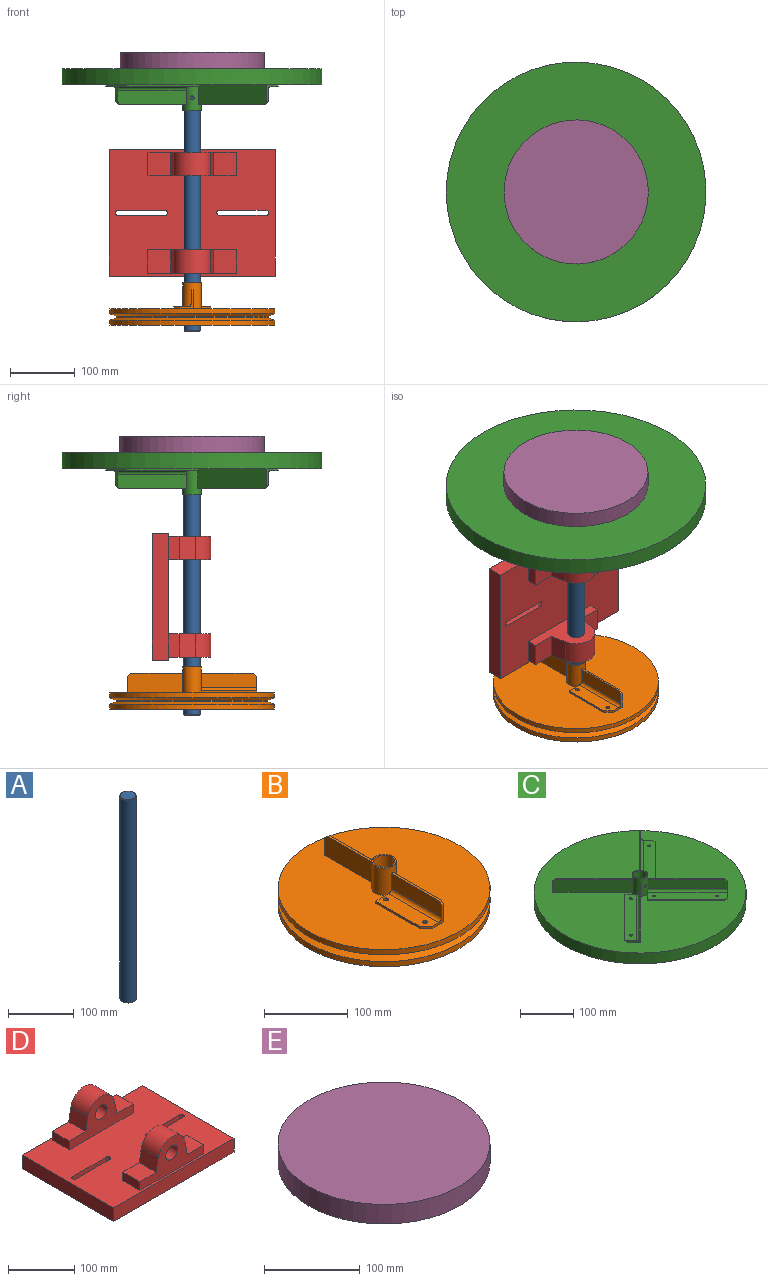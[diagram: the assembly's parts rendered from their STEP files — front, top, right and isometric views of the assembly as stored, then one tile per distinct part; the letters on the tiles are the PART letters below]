
ASSEMBLY  parts=5 mates=4
PART A: 5 faces, bbox 25x25x380 mm
  f0: cylinder r=12.5mm len=378mm, axis (0,0,-1), area 29688.1mm2, adj f3,f4
  f1: plane 23x23mm, normal (0,0,1), area 415.5mm2, adj f3
  f2: plane 23x23mm, normal (0,0,-1), area 415.5mm2, adj f4
  f3: cone r=11.5mm half-angle=45deg, axis (0,0,-1), area 106.6mm2, adj f0,f1
  f4: cone r=12.5mm half-angle=45deg, axis (0,0,1), area 106.6mm2, adj f0,f2
PART B: 41 faces, bbox 254x254x65 mm
  f0: plane 254x254mm, normal (0,0,1), area 45010.4mm2, adj f1,f8,f9,f10,f14,f15,f19,f21
  f1: cylinder r=127mm len=254mm, axis (0,0,1), area 5984.7mm2, adj f0,f2
  f2: cone r=127mm half-angle=70deg, axis (0,0,1), area 8157.4mm2, adj f1,f3
  f3: cylinder r=117mm len=234mm, axis (0,0,1), area 2000mm2, adj f2,f4
  f4: cone r=127mm half-angle=70deg, axis (0,0,-1), area 8157.4mm2, adj f3,f5
  f5: cylinder r=127mm len=254mm, axis (0,0,1), area 5984.7mm2, adj f4,f6
  f6: plane 254x254mm, normal (0,0,-1), area 50179.9mm2, adj f5,f7
  f7: cylinder r=12.5mm len=65mm, axis (0,0,1), area 5076.6mm2, adj f6,f35,f36
  f8: plane 30x27.3mm, normal (0,-1,0), area 95.3mm2, adj f0,f11,f12,f13,f14,f16,f21
  f9: plane 30x0.3mm, normal (0,-1,0), area 8.9mm2, adj f0,f10,f11,f21
  f10: plane 85x30mm, normal (-1,0,0), area 2537.5mm2, adj f0,f9,f11,f15,f20
  f11: plane 80x3mm, normal (0,0,1), area 239.9mm2, adj f8,f9,f10,f12,f20,f21
  f12: plane 85x22mm, normal (1,0,0), area 1857.5mm2, adj f8,f11,f15,f16,f20
  f13: plane 85x22mm, normal (0,0,1), area 1763.5mm2, adj f8,f14,f15,f16,f17,f18,f19
  f14: plane 75x3mm, normal (1,0,0), area 225mm2, adj f0,f8,f13,f19
  f15: plane 25x20mm, normal (0,1,0), area 131.4mm2, adj f0,f10,f12,f13,f16,f19,f20
  f16: cylinder r=5mm len=85mm, axis (0,1,0), area 667.6mm2, adj f8,f12,f13,f15
  f17: cylinder r=3mm len=6mm, axis (0,0,1), area 56.5mm2, adj f13,f38
  f18: cylinder r=3mm len=6mm, axis (0,0,1), area 56.5mm2, adj f13,f39
  f19: plane 10x10mm, normal (0.71,0.71,0), area 42.4mm2, adj f0,f13,f14,f15
  f20: plane 5x5mm, normal (0,0.71,0.71), area 21.2mm2, adj f10,f11,f12,f15
  f21: cylinder r=14.5mm len=40mm, axis (0,0,-1), area 3471.2mm2, adj f0,f8,f9,f11,f22,f23,f25,f35
  f22: plane 30x27.3mm, normal (0,1,0), area 95.3mm2, adj f0,f21,f25,f26,f27,f28,f30
  f23: plane 30x0.3mm, normal (0,1,0), area 8.9mm2, adj f0,f21,f24,f25
  f24: plane 85x30mm, normal (1,0,0), area 2537.5mm2, adj f0,f23,f25,f29,f34
  f25: plane 80x3mm, normal (0,0,1), area 239.9mm2, adj f21,f22,f23,f24,f26,f34
  f26: plane 85x22mm, normal (-1,0,0), area 1857.5mm2, adj f22,f25,f29,f30,f34
  f27: plane 85x22mm, normal (0,0,1), area 1763.5mm2, adj f22,f28,f29,f30,f31,f32,f33
  f28: plane 75x3mm, normal (-1,0,0), area 225mm2, adj f0,f22,f27,f33
  f29: plane 25x20mm, normal (0,-1,0), area 131.4mm2, adj f0,f24,f26,f27,f30,f33,f34
  f30: cylinder r=5mm len=85mm, axis (0,-1,0), area 667.6mm2, adj f22,f26,f27,f29
  f31: cylinder r=3mm len=6mm, axis (0,0,1), area 56.5mm2, adj f27,f40
  f32: cylinder r=3mm len=6mm, axis (0,0,1), area 56.5mm2, adj f27,f37
  f33: plane 10x10mm, normal (-0.71,-0.71,0), area 42.4mm2, adj f0,f27,f28,f29
  f34: plane 5x5mm, normal (0,-0.71,0.71), area 21.2mm2, adj f24,f25,f26,f29
  f35: plane 29x29mm, normal (0,0,1), area 169.6mm2, adj f7,f21
  f36: cylinder r=3mm len=6mm, axis (-1,0,0), area 38.2mm2, adj f7,f21
  f37: plane 6x6mm, normal (0,0,1), area 28.3mm2, adj f32
  f38: plane 6x6mm, normal (0,0,1), area 28.3mm2, adj f17
  f39: plane 6x6mm, normal (0,0,1), area 28.3mm2, adj f18
  f40: plane 6x6mm, normal (0,0,1), area 28.3mm2, adj f31
PART C: 64 faces, bbox 400x400x65 mm
  f0: plane 106.05x106.05mm, normal (-0.71,-0.71,0), area 3287mm2, adj f1,f16,f19,f23,f59
  f1: cylinder r=5mm len=109.6mm, axis (0.71,-0.71,0), area 1178.1mm2, adj f0,f9,f17,f19,f59
  f2: plane 106.05x106.05mm, normal (0.71,0.71,0), area 3287mm2, adj f3,f26,f29,f33,f59
  f3: cylinder r=5mm len=109.6mm, axis (-0.71,0.71,0), area 1178.1mm2, adj f2,f11,f27,f29,f59
  f4: cylinder r=5mm len=109.6mm, axis (-0.71,-0.71,0), area 1178.1mm2, adj f5,f12,f42,f44,f59
  f5: plane 106.05x106.05mm, normal (-0.71,0.71,0), area 3287mm2, adj f4,f38,f42,f45,f59
  f6: cylinder r=5mm len=109.6mm, axis (0.71,0.71,0), area 1178.1mm2, adj f7,f14,f52,f54,f59
  f7: plane 106.05x106.05mm, normal (0.71,-0.71,0), area 3287mm2, adj f6,f48,f52,f55,f59
  f8: plane 106.05x106.05mm, normal (0.71,0.71,0), area 4486.8mm2, adj f16,f19,f23,f56,f59
  f9: plane 18.95x18.95mm, normal (-0.71,0.71,0), area 85mm2, adj f1,f17,f18,f56,f59
  f10: plane 106.05x106.05mm, normal (-0.71,-0.71,0), area 4486.8mm2, adj f26,f29,f33,f56,f59
  f11: plane 18.95x18.95mm, normal (0.71,-0.71,0), area 85mm2, adj f3,f27,f28,f56,f59
  f12: plane 18.95x18.95mm, normal (0.71,0.71,0), area 85mm2, adj f4,f43,f44,f56,f59
  f13: plane 106.05x106.05mm, normal (0.71,-0.71,0), area 4486.8mm2, adj f38,f42,f45,f56,f59
  f14: plane 18.95x18.95mm, normal (-0.71,-0.71,0), area 85mm2, adj f6,f53,f54,f56,f59
  f15: plane 106.05x106.05mm, normal (-0.71,0.71,0), area 4486.8mm2, adj f48,f52,f55,f56,f59
  f16: plane 104.64x104.64mm, normal (0,0,1), area 434.8mm2, adj f0,f8,f23,f59
  f17: plane 121.62x118.09mm, normal (0,0,1), area 3231mm2, adj f1,f9,f18,f19,f20,f21,f22
  f18: plane 102.53x102.53mm, normal (-0.71,-0.71,0), area 435mm2, adj f9,f17,f22,f56
  f19: plane 25x17.68mm, normal (0.71,-0.71,0), area 146.4mm2, adj f0,f1,f8,f17,f22,f23,f56
  f20: cylinder r=3mm len=6mm, axis (0,0,1), area 56.5mm2, adj f17,f58
  f21: cylinder r=3mm len=6mm, axis (0,0,1), area 56.5mm2, adj f17,f57
  f22: plane 7.07x3mm, normal (0,-1,0), area 21.2mm2, adj f17,f18,f19,f56
  f23: plane 5.66x5.66mm, normal (0.5,-0.5,0.71), area 21.2mm2, adj f0,f8,f16,f19
  f24: plane 6x6mm, normal (0,0,1), area 28.3mm2, adj f51
  f25: plane 6x6mm, normal (0,0,1), area 28.3mm2, adj f50
  f26: plane 104.64x104.64mm, normal (0,0,1), area 434.8mm2, adj f2,f10,f33,f59
  f27: plane 121.62x118.09mm, normal (0,0,1), area 3231mm2, adj f3,f11,f28,f29,f30,f31,f32
  f28: plane 102.53x102.53mm, normal (0.71,0.71,0), area 435mm2, adj f11,f27,f32,f56
  f29: plane 25x17.68mm, normal (-0.71,0.71,0), area 146.4mm2, adj f2,f3,f10,f27,f32,f33,f56
  f30: cylinder r=3mm len=6mm, axis (0,0,1), area 56.5mm2, adj f27,f47
  f31: cylinder r=3mm len=6mm, axis (0,0,1), area 56.5mm2, adj f27,f46
  f32: plane 7.07x3mm, normal (0,1,0), area 21.2mm2, adj f27,f28,f29,f56
  f33: plane 5.66x5.66mm, normal (-0.5,0.5,0.71), area 21.2mm2, adj f2,f10,f26,f29
  f34: plane 6x6mm, normal (0,0,1), area 28.3mm2, adj f40
  f35: plane 6x6mm, normal (0,0,1), area 28.3mm2, adj f41
  f36: cylinder r=200mm len=400mm, axis (0,0,1), area 31415.9mm2, adj f37,f56
  f37: plane 400x400mm, normal (0,0,-1), area 125663.7mm2, adj f36
  f38: plane 5.66x5.66mm, normal (-0.5,-0.5,0.71), area 21.2mm2, adj f5,f13,f42,f45
  f39: plane 7.07x3mm, normal (-1,0,0), area 21.2mm2, adj f42,f43,f44,f56
  f40: cylinder r=3mm len=6mm, axis (0,0,1), area 56.5mm2, adj f34,f44
  f41: cylinder r=3mm len=6mm, axis (0,0,1), area 56.5mm2, adj f35,f44
  f42: plane 25x17.68mm, normal (-0.71,-0.71,0), area 146.4mm2, adj f4,f5,f13,f38,f39,f44,f56
  f43: plane 102.53x102.53mm, normal (-0.71,0.71,0), area 435mm2, adj f12,f39,f44,f56
  f44: plane 121.62x118.09mm, normal (0,0,1), area 3231mm2, adj f4,f12,f39,f40,f41,f42,f43
  f45: plane 104.64x104.64mm, normal (0,0,1), area 434.8mm2, adj f5,f13,f38,f59
  f46: plane 6x6mm, normal (0,0,1), area 28.3mm2, adj f31
  f47: plane 6x6mm, normal (0,0,1), area 28.3mm2, adj f30
  f48: plane 5.66x5.66mm, normal (0.5,0.5,0.71), area 21.2mm2, adj f7,f15,f52,f55
  f49: plane 7.07x3mm, normal (1,0,0), area 21.2mm2, adj f52,f53,f54,f56
  f50: cylinder r=3mm len=6mm, axis (0,0,1), area 56.5mm2, adj f25,f54
  f51: cylinder r=3mm len=6mm, axis (0,0,1), area 56.5mm2, adj f24,f54
  f52: plane 25x17.68mm, normal (0.71,0.71,0), area 146.4mm2, adj f6,f7,f15,f48,f49,f54,f56
  f53: plane 102.53x102.53mm, normal (0.71,-0.71,0), area 435mm2, adj f14,f49,f54,f56
  f54: plane 121.62x118.09mm, normal (0,0,1), area 3231mm2, adj f6,f14,f49,f50,f51,f52,f53
  f55: plane 104.64x104.64mm, normal (0,0,1), area 434.8mm2, adj f7,f15,f48,f59
  f56: plane 400x400mm, normal (0,0,1), area 107058.6mm2, adj f8,f9,f10,f11,f12,f13,f14,f15
  f57: plane 6x6mm, normal (0,0,1), area 28.3mm2, adj f21
  f58: plane 6x6mm, normal (0,0,1), area 28.3mm2, adj f20
  f59: cylinder r=14.45mm len=40mm, axis (0,0,-1), area 3236.8mm2, adj f0,f1,f2,f3,f4,f5,f6,f7
  f60: cylinder r=12.5mm len=40mm, axis (0,0,-1), area 3113.1mm2, adj f61,f62,f63
  f61: plane 28.9x28.9mm, normal (0,0,1), area 165.1mm2, adj f59,f60
  f62: cylinder r=3mm len=6mm, axis (0,-1,0), area 37.2mm2, adj f59,f60
  f63: plane 25x25mm, normal (0,0,1), area 490.9mm2, adj f60
PART D: 34 faces, bbox 256x195x90 mm
  f0: plane 36x35.03mm, normal (0,0,1), area 1260.9mm2, adj f1,f6,f8,f9
  f1: plane 36x16mm, normal (-1,0,0), area 576mm2, adj f0,f8,f9,f10
  f2: plane 36x16mm, normal (1,0,0), area 576mm2, adj f3,f8,f9,f10
  f3: plane 36x35.03mm, normal (0,0,1), area 1260.9mm2, adj f2,f4,f8,f9
  f4: plane 36x25.04mm, normal (0.98,0,0.17), area 915.2mm2, adj f3,f5,f8,f9
  f5: cylinder r=29mm len=57.12mm, axis (0,-1,0), area 2915.4mm2, adj f4,f6,f8,f9
  f6: plane 36x25.04mm, normal (-0.98,0,0.17), area 915.2mm2, adj f0,f5,f8,f9
  f7: cylinder r=12.5mm len=36mm, axis (0,-1,0), area 2827.4mm2, adj f8,f9
  f8: plane 136x65mm, normal (0,1,0), area 4256.1mm2, adj f0,f1,f2,f3,f4,f5,f6,f7
  f9: plane 136x65mm, normal (0,-1,0), area 4256.1mm2, adj f0,f1,f2,f3,f4,f5,f6,f7
  f10: plane 256x195mm, normal (0,0,1), area 38875.5mm2, adj f1,f2,f8,f9,f12,f13,f19,f20
  f11: plane 36x35.03mm, normal (0,0,1), area 1260.9mm2, adj f12,f17,f19,f20
  f12: plane 36x16mm, normal (-1,0,0), area 576mm2, adj f10,f11,f19,f20
  f13: plane 36x16mm, normal (1,0,0), area 576mm2, adj f10,f14,f19,f20
  f14: plane 36x35.03mm, normal (0,0,1), area 1260.9mm2, adj f13,f15,f19,f20
  f15: plane 36x25.04mm, normal (0.98,0,0.17), area 915.2mm2, adj f14,f16,f19,f20
  f16: cylinder r=29mm len=57.12mm, axis (0,-1,0), area 2915.4mm2, adj f15,f17,f19,f20
  f17: plane 36x25.04mm, normal (-0.98,0,0.17), area 915.2mm2, adj f11,f16,f19,f20
  f18: cylinder r=12.5mm len=36mm, axis (0,-1,0), area 2827.4mm2, adj f19,f20
  f19: plane 136x65mm, normal (0,1,0), area 4256.1mm2, adj f10,f11,f12,f13,f14,f15,f16,f17
  f20: plane 136x65mm, normal (0,-1,0), area 4256.1mm2, adj f10,f11,f12,f13,f14,f15,f16,f17
  f21: cylinder r=4mm len=25mm, axis (0,0,1), area 314.2mm2, adj f10,f22,f32,f33
  f22: plane 72x25mm, normal (0,-1,0), area 1800mm2, adj f10,f21,f23,f33
  f23: cylinder r=4mm len=25mm, axis (0,0,1), area 314.2mm2, adj f10,f22,f32,f33
  f24: plane 72x25mm, normal (0,-1,0), area 1800mm2, adj f10,f25,f30,f33
  f25: cylinder r=4mm len=25mm, axis (0,0,1), area 314.2mm2, adj f10,f24,f26,f33
  f26: plane 72x25mm, normal (0,1,0), area 1800mm2, adj f10,f25,f30,f33
  f27: plane 195x25mm, normal (1,0,0), area 4875mm2, adj f10,f28,f31,f33
  f28: plane 256x25mm, normal (0,-1,0), area 6400mm2, adj f10,f27,f29,f33
  f29: plane 195x25mm, normal (-1,0,0), area 4875mm2, adj f10,f28,f31,f33
  f30: cylinder r=4mm len=25mm, axis (0,0,1), area 314.2mm2, adj f10,f24,f26,f33
  f31: plane 256x25mm, normal (0,1,0), area 6400mm2, adj f10,f27,f29,f33
  f32: plane 72x25mm, normal (0,1,0), area 1800mm2, adj f10,f21,f23,f33
  f33: plane 256x195mm, normal (0,0,-1), area 48667.5mm2, adj f21,f22,f23,f24,f25,f26,f27,f28
PART E: 3 faces, bbox 222x222x25 mm
  f0: plane 222x222mm, normal (0,0,1), area 38707.6mm2, adj f1
  f1: cylinder r=111mm len=222mm, axis (0,0,-1), area 17435.8mm2, adj f0,f2
  f2: sphere r=2222mm, area 38731.7mm2, adj f1
PLACE A t=(-414.59,-128.41,249.48)mm
PLACE B t=(-414.59,-128.41,259.48)mm
PLACE C rot(axis=(0,1,0),180deg) t=(-414.59,-128.41,654.48)mm
PLACE D rot(axis=(0,-0.71,0.71),180deg) t=(-414.59,-128.41,375.48)mm
PLACE E t=(-414.59,-128.41,679.48)mm
MATE fastened A.f0 <-> C.f60  axis (0,0,1) through (-414.59,-128.41,629.48)mm
MATE fastened B.f1 <-> D.f7  axis (0,0,-1) through (-414.59,-128.41,259.48)mm
MATE fastened A.f0 <-> B.f1  axis (0,0,-1) through (-414.59,-128.41,249.48)mm
MATE fastened C.f36 <-> E.f1  axis (0,0,1) through (-414.59,-128.41,654.48)mm
